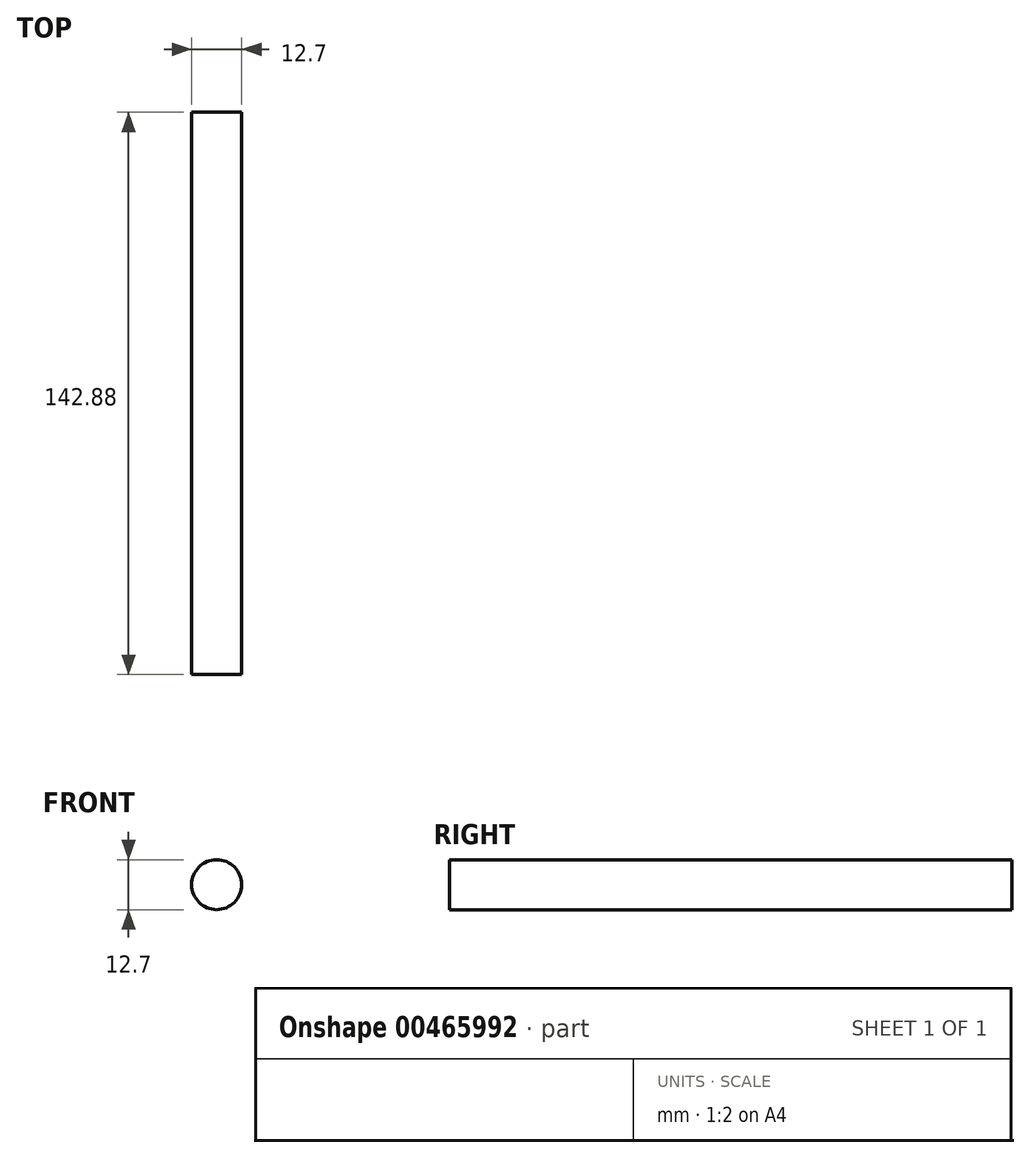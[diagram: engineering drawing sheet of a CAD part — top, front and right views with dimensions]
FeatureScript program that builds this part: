
annotation { "Feature Type Name" : "Feature", "Feature Type Description" : "" }
export const myFeature = defineFeature(function(context is Context, id is Id, definition is map)
    precondition{}
    {
        {
            var Q0;
            Q0=qCreatedBy(makeId("Front.planeOp"),FACE);
            var sketch = newSketch(context, id + "F0", { "sketchPlane" : qUnion([Q0])});
            skCircle(sketch, "E0", {"center": v(0, 0) * mm, "radius": 6.35 * mm});
            skSolve(sketch);
        }
        {
            var Q0;
            Q0 = qSketchRegion(id + "F0", true);
            extrude(context, id + "F1", {"entities" : qUnion([Q0]), "depth" : 142.88 * mm});
        }
    });
